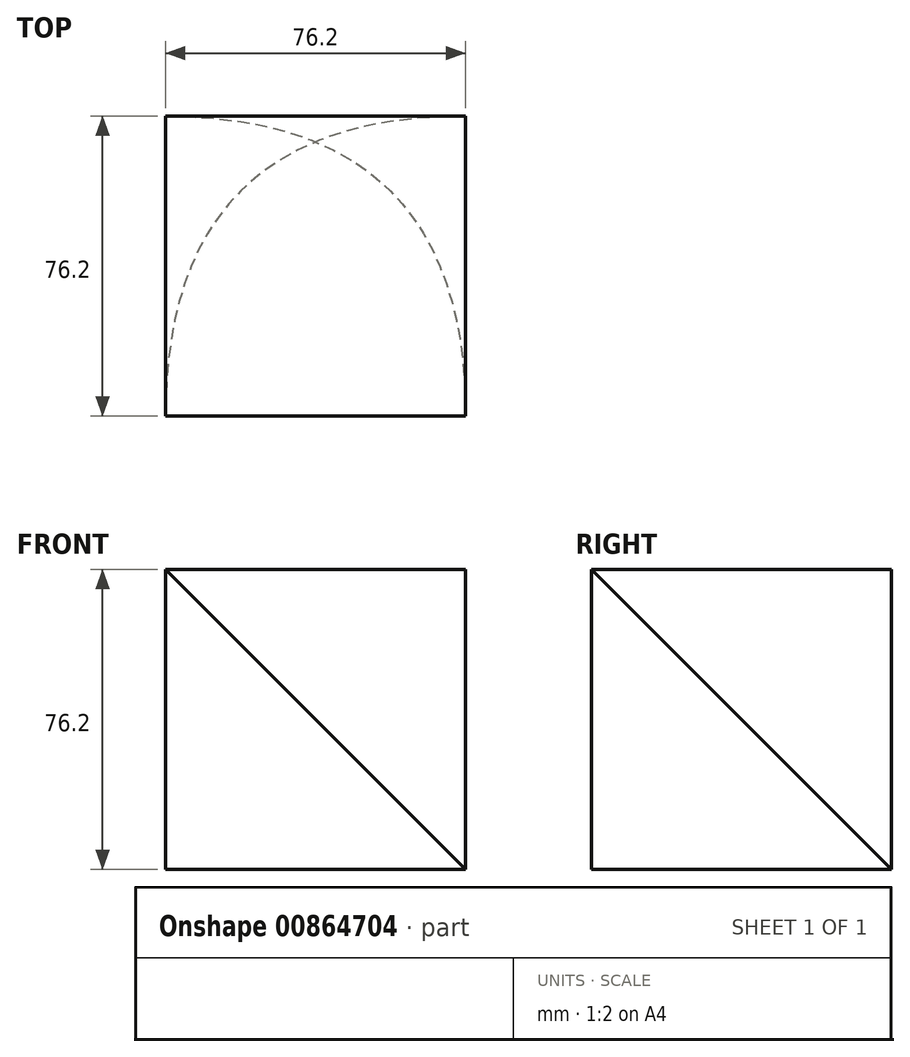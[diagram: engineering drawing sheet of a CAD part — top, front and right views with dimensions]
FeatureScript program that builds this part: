
annotation { "Feature Type Name" : "Feature", "Feature Type Description" : "" }
export const myFeature = defineFeature(function(context is Context, id is Id, definition is map)
    precondition{}
    {
        {
            var Q0;
            Q0=qCreatedBy(makeId("Top.planeOp"),FACE);
            var sketch = newSketch(context, id + "F0", { "sketchPlane" : qUnion([Q0])});
            skLineSegment(sketch, "E0.bottom", {"start": v(38.1, 38.1) * mm, "end": v(-38.1, 38.1) * mm});
            skLineSegment(sketch, "E0.top", {"start": v(38.1, -38.1) * mm, "end": v(-38.1, -38.1) * mm});
            skLineSegment(sketch, "E0.left", {"start": v(38.1, 38.1) * mm, "end": v(38.1, -38.1) * mm});
            skLineSegment(sketch, "E0.right", {"start": v(-38.1, 38.1) * mm, "end": v(-38.1, -38.1) * mm});
            skPoint(sketch, "E0.middle", {"position": v(0, 0) * mm});
            skSolve(sketch);
        }
        {
            var Q0;
            Q0=qCreatedBy(makeId("Top.planeOp"),FACE);
            cPlane(context, id + "F1", {"entities" : qUnion([Q0]), "cplaneType" : CPlaneType.OFFSET, "offset" : 38.1 * mm, "width" : 152.4 * mm, "height" : 152.4 * mm});
        }
        {
            var Q0;
            Q0=qCreatedBy(id+"F1.planeOp",FACE);
            cPlane(context, id + "F2", {"entities" : qUnion([Q0]), "cplaneType" : CPlaneType.OFFSET, "offset" : 38.1 * mm, "width" : 152.4 * mm, "height" : 152.4 * mm});
        }
        {
            var Q0;
            Q0=qCreatedBy(id+"F2.planeOp",FACE);
            var sketch = newSketch(context, id + "F3", { "sketchPlane" : qUnion([Q0])});
            skLineSegment(sketch, "E1.bottom", {"start": v(38.1, 38.1) * mm, "end": v(-38.1, 38.1) * mm});
            skLineSegment(sketch, "E1.top", {"start": v(38.1, -38.1) * mm, "end": v(-38.1, -38.1) * mm});
            skLineSegment(sketch, "E1.left", {"start": v(38.1, 38.1) * mm, "end": v(38.1, -38.1) * mm});
            skLineSegment(sketch, "E1.right", {"start": v(-38.1, 38.1) * mm, "end": v(-38.1, -38.1) * mm});
            skPoint(sketch, "E1.middle", {"position": v(0, 0) * mm});
            skSolve(sketch);
        }
        {
            var Q0;
            Q0=makeQuery(id+"F0.imprint","IMPRINT",FACE,{"disambiguationData":[TD([[makeQuery(id+"F0.imprint","IMPRINT",EDGE,{"derivedFrom":sQuery(id+"F0.wireOp",EDGE,"E0.bottom")}),1.0]])]});
            var Q1;
            Q1=makeQuery(id+"F3.imprint","IMPRINT",FACE,{"disambiguationData":[TD([[makeQuery(id+"F3.imprint","IMPRINT",EDGE,{"derivedFrom":sQuery(id+"F3.wireOp",EDGE,"E1.bottom")}),1.0]])]});
            var Q2;
            Q2=sQuery(id+"F0.wireOp",VERTEX,"E0.top.end");
            var Q3;
            Q3=sQuery(id+"F3.wireOp",VERTEX,"E1.bottom.end");
            loft(context, id + "F4", {"sheetProfilesArray" : [{ "sheetProfileEntities" : qUnion([Q0]) }, { "sheetProfileEntities" : qUnion([Q1]) }], "matchConnections" : true, "connections" : [{ "connectionEntities" : qUnion([Q2, Q3]), "connectionEdgeQueries" : qUnion([]), "connectionEdgeParameters" : [] }]});
        }
    });
